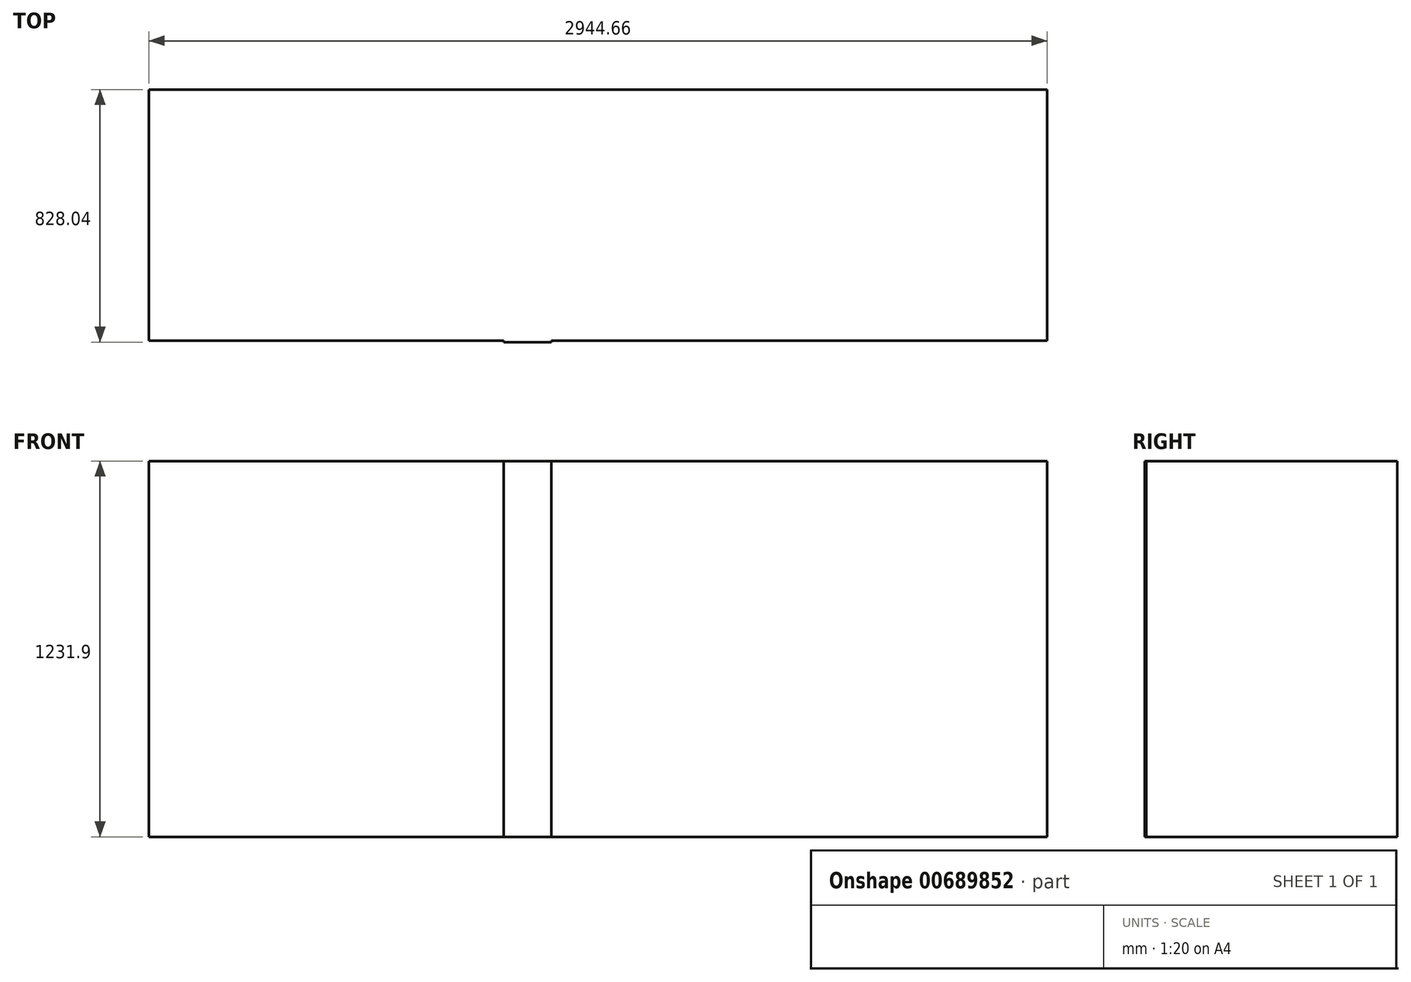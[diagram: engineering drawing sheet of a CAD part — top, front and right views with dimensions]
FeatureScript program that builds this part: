
annotation { "Feature Type Name" : "Feature", "Feature Type Description" : "" }
export const myFeature = defineFeature(function(context is Context, id is Id, definition is map)
    precondition{}
    {
        {
            var Q0;
            Q0=qCreatedBy(makeId("Top.planeOp"),FACE);
            var sketch = newSketch(context, id + "F0", { "sketchPlane" : qUnion([Q0])});
            skSolve(sketch);
        }
        {
            var Q0;
            Q0=qCreatedBy(makeId("Top.planeOp"),FACE);
            var sketch = newSketch(context, id + "F1", { "sketchPlane" : qUnion([Q0])});
            skLineSegment(sketch, "E0.bottom", {"start": v(21.04, 0) * mm, "end": v(1184.54, 0) * mm});
            skLineSegment(sketch, "E0.top", {"start": v(21.04, 822.96) * mm, "end": v(2965.7, 822.96) * mm});
            skLineSegment(sketch, "E0.left", {"start": v(21.04, 0) * mm, "end": v(21.04, 822.96) * mm});
            skLineSegment(sketch, "E0.right", {"start": v(2965.7, 0) * mm, "end": v(2965.7, 822.96) * mm});
            skLineSegment(sketch, "E1.top", {"start": v(1184.54, -5.08) * mm, "end": v(1340.4, -5.08) * mm});
            skLineSegment(sketch, "E1.left", {"start": v(1184.54, 0) * mm, "end": v(1184.54, -5.08) * mm});
            skLineSegment(sketch, "E1.right", {"start": v(1340.4, 0) * mm, "end": v(1340.4, -5.08) * mm});
            skLineSegment(sketch, "E2.trimOffspring", {"start": v(1340.4, 0) * mm, "end": v(2965.7, 0) * mm});
            skSolve(sketch);
        }
        {
            var Q0;
            Q0 = qSketchRegion(id + "F1", true);
            extrude(context, id + "F2", {"entities" : qUnion([Q0]), "depth" : 1231.9 * mm, "offsetDistance" : 25.4 * mm});
        }
    });
